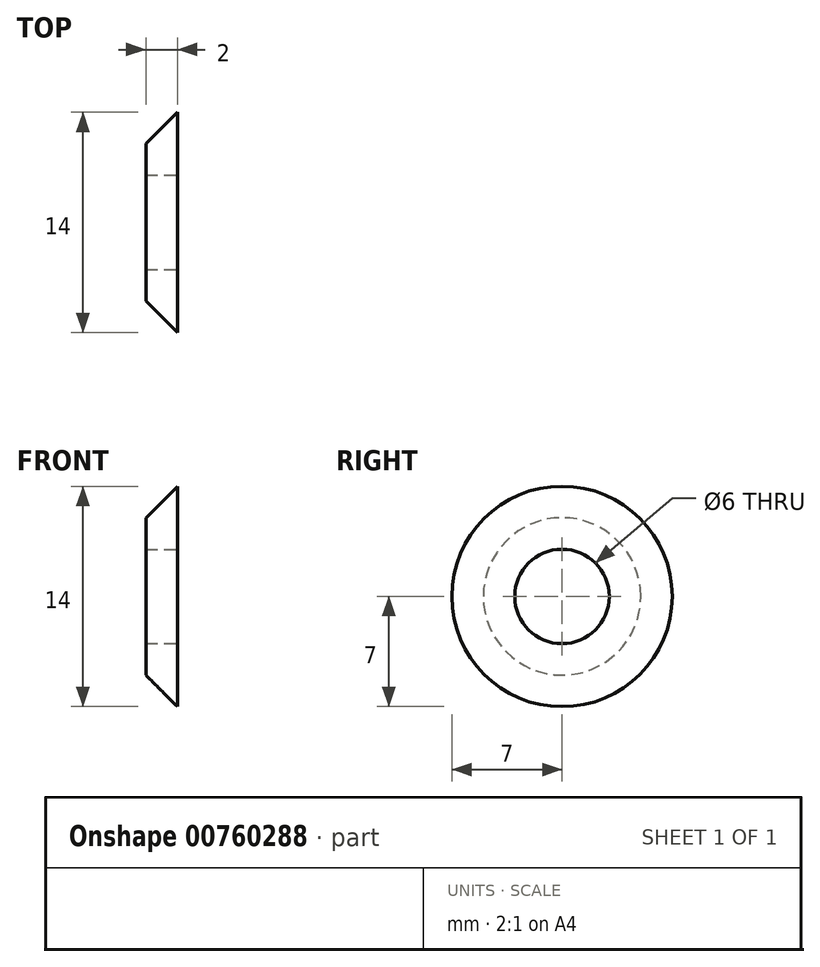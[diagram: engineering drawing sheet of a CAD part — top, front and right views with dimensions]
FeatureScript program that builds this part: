
annotation { "Feature Type Name" : "Feature", "Feature Type Description" : "" }
export const myFeature = defineFeature(function(context is Context, id is Id, definition is map)
    precondition{}
    {
        {
            var Q0;
            Q0=qCreatedBy(makeId("Top.planeOp"),FACE);
            var sketch = newSketch(context, id + "F0", { "sketchPlane" : qUnion([Q0])});
            skLineSegment(sketch, "E0", {"start": v(0, 0) * mm, "end": v(-2, 0) * mm});
            skLineSegment(sketch, "E1", {"start": v(-2, 0) * mm, "end": v(-2, 5) * mm});
            skLineSegment(sketch, "E2", {"start": v(-2, 5) * mm, "end": v(0, 7) * mm});
            skLineSegment(sketch, "E3", {"start": v(0, 7) * mm, "end": v(0, 0) * mm});
            skSolve(sketch);
        }
        {
            var Q0;
            Q0=makeQuery(id+"F0.imprint","IMPRINT",FACE,{"disambiguationData":[TD([[makeQuery(id+"F0.imprint","IMPRINT",EDGE,{"derivedFrom":sQuery(id+"F0.wireOp",EDGE,"E0")}),-1.0]])]});
            var Q1;
            Q1=sQuery(id+"F0.wireOp",EDGE,"E0");
            revolve(context, id + "F1", {"surfaceOperationType" : NewSurfaceOperationType.NEW, "entities" : qUnion([Q0]), "axis" : qUnion([Q1]), "revolveType" : RevolveType.FULL});
        }
        {
            var Q0;
            Q0=makeQuery(id+"F1.opRevolve","SWEPT_FACE",FACE,{"disambiguationData":[OSD([sQuery(id+"F0.wireOp",EDGE,"E3")])]});
            var sketch = newSketch(context, id + "F2", { "sketchPlane" : qUnion([Q0])});
            skPoint(sketch, "E4", {"position": v(0, 0) * mm});
            skSolve(sketch);
        }
        {
            var Q0;
            Q0=sQuery(id+"F2.wireOp",VERTEX,"E4");
            var Q1;
            Q1=makeQuery(id+"F1.opRevolve","SWEPT_BODY",BODY,{"disambiguationData":[OSD([sQuery(id+"F0.wireOp",EDGE,"E0"),sQuery(id+"F0.wireOp",EDGE,"E1"),sQuery(id+"F0.wireOp",EDGE,"E2"),sQuery(id+"F0.wireOp",EDGE,"E3")])]});
            hole(context, id + "F3", {"style" : HoleStyle.SIMPLE, "endStyle" : HoleEndStyle.THROUGH, "holeDiameter" : 6 * mm, "majorDiameter" : 5 * mm, "isTappedThrough" : true, "tappedDepth" : 12 * mm, "tapClearance" : 3, "locations" : qUnion([Q0]), "scope" : qUnion([Q1])});
        }
    });
